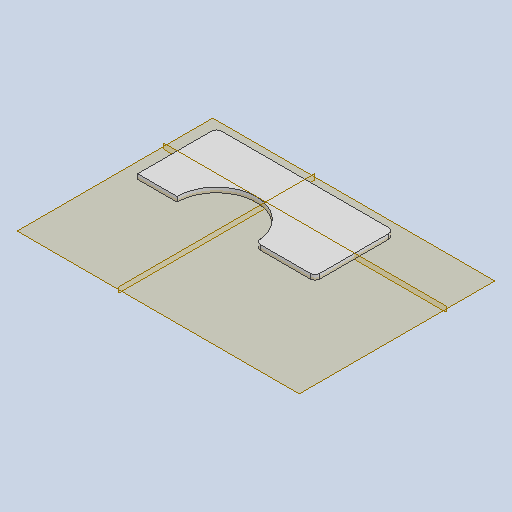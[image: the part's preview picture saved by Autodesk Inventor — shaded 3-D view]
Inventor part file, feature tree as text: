
AUTODESK INVENTOR PART (.ipt)
format: ipt  version: 2025.2 (Build 292293000, 293)  size: 129,024 bytes
history: native  units: mm
features: sketch x2, other x1, extrude x1
ambient origin geometry x8: Origin, YZ Plane, XZ Plane, XY Plane, X Axis, Y Axis, Z Axis, Center Point
bodies: Body1 (feature_tree)
feature tree (4):
  other  "Sólido1"
  sketch  "Esboço1"  dims[d0=800.0mm d1=1800.0mm]
  extrude  "Extrusão1"  Depth=1800.0mm
  sketch  "Esboço3"  dims[d3=650.0mm d5=15.0mm d6=800.0mm d7=1800.0mm d9=250.0mm d11=800.0mm d13=400.0mm d14=400.0mm d15=400.0mm d16=1800.0mm d17=800.0mm d19=400.0mm d20=50.0mm d21=800.0mm d22=50.0mm d23=0.0mm d24=0.5mm d25=0.872665mm]
